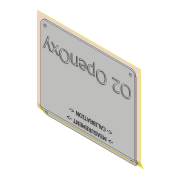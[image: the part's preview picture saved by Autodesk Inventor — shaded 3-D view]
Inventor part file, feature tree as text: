
AUTODESK INVENTOR PART (.ipt)
format: ipt  version: 2019.4 (Build 234330000, 330)  size: 747,520 bytes
history: native  units: mm
features: extrude x3, sketch x3, plane x2, reference x2, other x2, projected_geometry x1
ambient origin geometry x8: Origin, YZ Plane, XZ Plane, XY Plane, X Axis, Y Axis, Z Axis, Center Point
bodies: Solid1 (feature_tree)
feature tree (13):
  plane  "Work Plane1"
  extrude  "Extrusion1"  Depth=1.5mm TaperAngle=0.0deg
  plane  "Work Plane2"
  extrude  "Extrusion2"  [1 undecoded]
  extrude  "Extrusion3"  [1 undecoded]
  sketch  "Sketch1"  dims[d0=1.5mm d1=0.0mm d2=1.5mm d3=0.0mm]
  reference  "Reference1"
  sketch  "Sketch2"  dims[d4=0.5mm d5=0.0mm]
  reference  "Reference2"
  sketch  "Sketch3"
  projected_geometry  "Projected Loop1"
  other  "Assemlby_OpenOxygen.iam"
  other  "03_OpenOxygen_Box:1"
note: 2 required parameter values undecoded (feature->parameter linkage not recoverable at this tier; creation-order binding heuristic only, values carry confidence <= 0.55)
